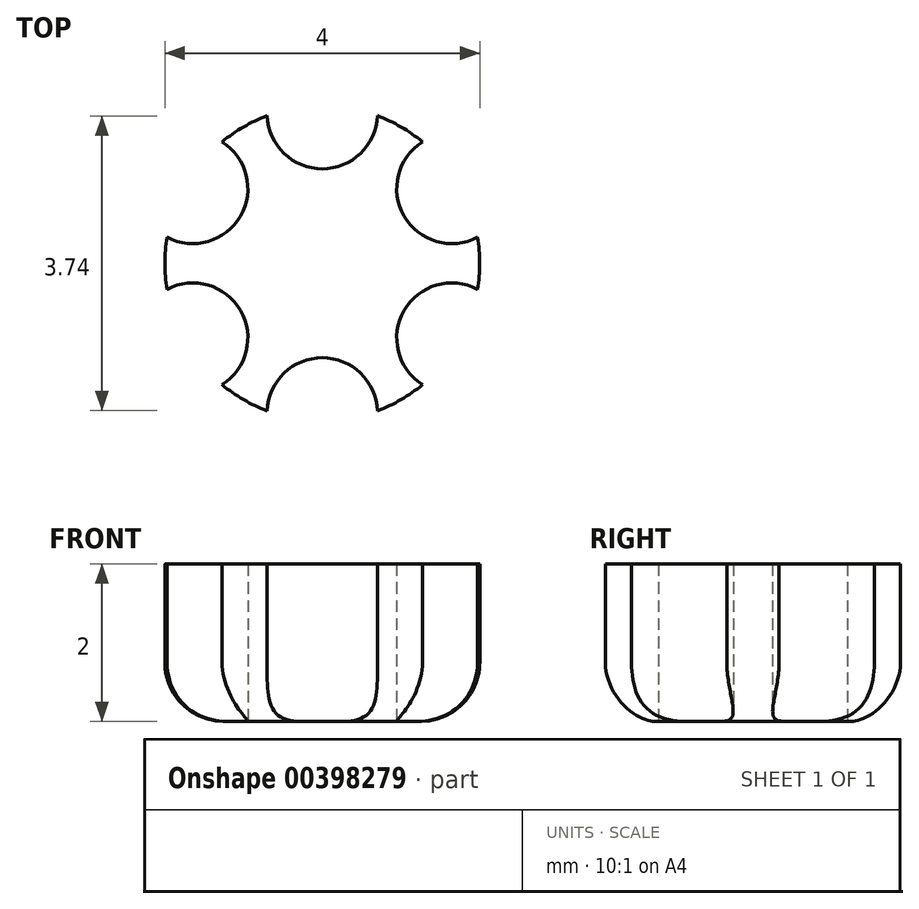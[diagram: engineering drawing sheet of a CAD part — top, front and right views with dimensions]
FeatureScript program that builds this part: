
annotation { "Feature Type Name" : "Feature", "Feature Type Description" : "" }
export const myFeature = defineFeature(function(context is Context, id is Id, definition is map)
    precondition{}
    {
        {
            var Q0;
            Q0=qCreatedBy(makeId("Top.planeOp"),FACE);
            var sketch = newSketch(context, id + "F0", { "sketchPlane" : qUnion([Q0])});
            skArc(sketch, "E0", {"start": v(-0.7, 1.87) * mm, "mid": v(-1, 1.73) * mm, "end": v(-1.27, 1.54) * mm});
            skCircle(sketch, "E1", {"center": v(0, 0) * mm, "radius": 1.9 * mm, "construction": true});
            skLineSegment(sketch, "E2", {"start": v(2.22, 1.28) * mm, "end": v(-2.42, -1.4) * mm, "construction": true});
            skLineSegment(sketch, "E3", {"start": v(2.36, -1.36) * mm, "end": v(-2.72, 1.57) * mm, "construction": true});
            skLineSegment(sketch, "E4", {"start": v(0, 2.52) * mm, "end": v(0, -2.45) * mm, "construction": true});
            skArc(sketch, "E5", {"start": v(-0.7, 1.87) * mm, "mid": v(0, 1.2) * mm, "end": v(0.7, 1.87) * mm});
            skArc(sketch, "E6", {"start": v(-1.97, 0.33) * mm, "mid": v(-1.04, 0.6) * mm, "end": v(-1.27, 1.54) * mm});
            skArc(sketch, "E7", {"start": v(-1.27, -1.54) * mm, "mid": v(-1.04, -0.6) * mm, "end": v(-1.97, -0.33) * mm});
            skArc(sketch, "E8", {"start": v(0.7, -1.87) * mm, "mid": v(0, -1.2) * mm, "end": v(-0.7, -1.87) * mm});
            skArc(sketch, "E9", {"start": v(1.97, -0.33) * mm, "mid": v(1.04, -0.6) * mm, "end": v(1.27, -1.54) * mm});
            skArc(sketch, "E10", {"start": v(1.27, 1.54) * mm, "mid": v(1.04, 0.6) * mm, "end": v(1.97, 0.33) * mm});
            skArc(sketch, "E11.trimOffspring", {"start": v(-1.97, 0.33) * mm, "mid": v(-2, 0) * mm, "end": v(-1.97, -0.33) * mm});
            skArc(sketch, "E12.trimOffspring", {"start": v(-1.27, -1.54) * mm, "mid": v(-1, -1.73) * mm, "end": v(-0.7, -1.87) * mm});
            skArc(sketch, "E13.trimOffspring", {"start": v(0.7, -1.87) * mm, "mid": v(1, -1.73) * mm, "end": v(1.27, -1.54) * mm});
            skArc(sketch, "E14.trimOffspring", {"start": v(1.97, -0.33) * mm, "mid": v(2, 0) * mm, "end": v(1.97, 0.33) * mm});
            skArc(sketch, "E15.trimOffspring", {"start": v(1.27, 1.54) * mm, "mid": v(1, 1.73) * mm, "end": v(0.7, 1.87) * mm});
            skSolve(sketch);
        }
        {
            var Q0;
            Q0 = qSketchRegion(id + "F0", true);
            extrude(context, id + "F1", {"entities" : qUnion([Q0]), "depth" : 2 * mm});
        }
        {
            var Q0;
            Q0=qCreatedBy(makeId("Front.planeOp"),FACE);
            var sketch = newSketch(context, id + "F2", { "sketchPlane" : qUnion([Q0])});
            skLineSegment(sketch, "E16", {"start": v(-2, 0) * mm, "end": v(-2, 0.75) * mm});
            skLineSegment(sketch, "E17", {"start": v(0, 0) * mm, "end": v(0, 2.47) * mm, "construction": true});
            skLineSegment(sketch, "E18", {"start": v(-1.25, 0) * mm, "end": v(-2, 0) * mm});
            skArc(sketch, "E19", {"start": v(-2, 0.75) * mm, "mid": v(-1.78, 0.22) * mm, "end": v(-1.25, 0) * mm});
            skSolve(sketch);
        }
        {
            var Q0;
            Q0 = qSketchRegion(id + "F2", true);
            var Q1;
            Q1=sQuery(id+"F2.wireOp",EDGE,"E17");
            revolve(context, id + "F3", {"operationType" : NewBodyOperationType.REMOVE, "entities" : qUnion([Q0]), "axis" : qUnion([Q1]), "revolveType" : RevolveType.FULL, "oppositeDirection" : true});
        }
    });
